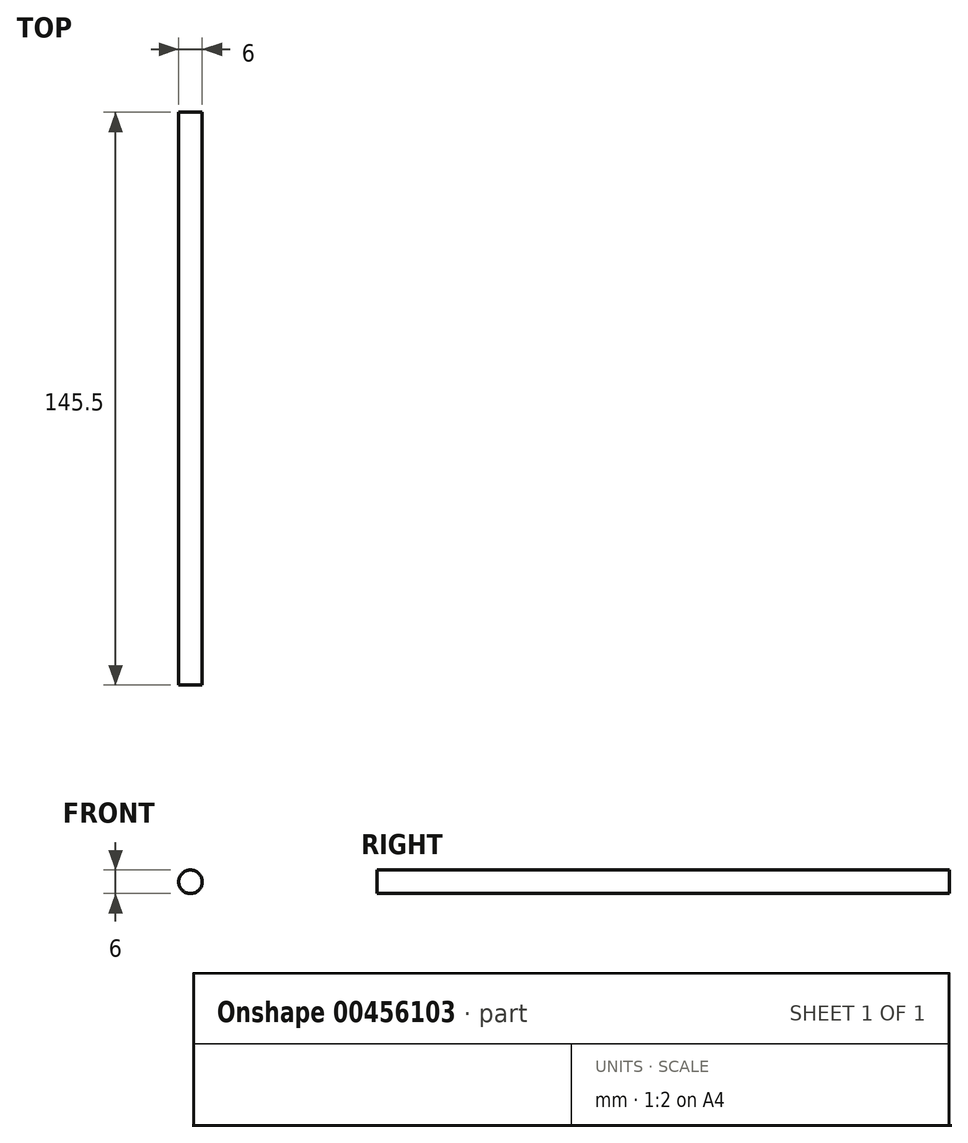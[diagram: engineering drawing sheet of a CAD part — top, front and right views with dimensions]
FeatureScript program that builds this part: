
annotation { "Feature Type Name" : "Feature", "Feature Type Description" : "" }
export const myFeature = defineFeature(function(context is Context, id is Id, definition is map)
    precondition{}
    {
        {
            var Q0;
            Q0=qCreatedBy(makeId("Front.planeOp"),FACE);
            var sketch = newSketch(context, id + "F0", { "sketchPlane" : qUnion([Q0])});
            skCircle(sketch, "E0", {"center": v(0, 0) * mm, "radius": 3 * mm});
            skSolve(sketch);
        }
        {
            var Q0;
            Q0=makeQuery(id+"F0.imprint","IMPRINT",FACE,{"disambiguationData":[TD([[makeQuery(id+"F0.imprint","IMPRINT",EDGE,{"derivedFrom":sQuery(id+"F0.wireOp",EDGE,"E0")}),1.0]])]});
            extrude(context, id + "F1", {"entities" : qUnion([Q0]), "oppositeDirection" : true, "depth" : 145.5 * mm, "offsetDistance" : 25 * mm});
        }
    });
